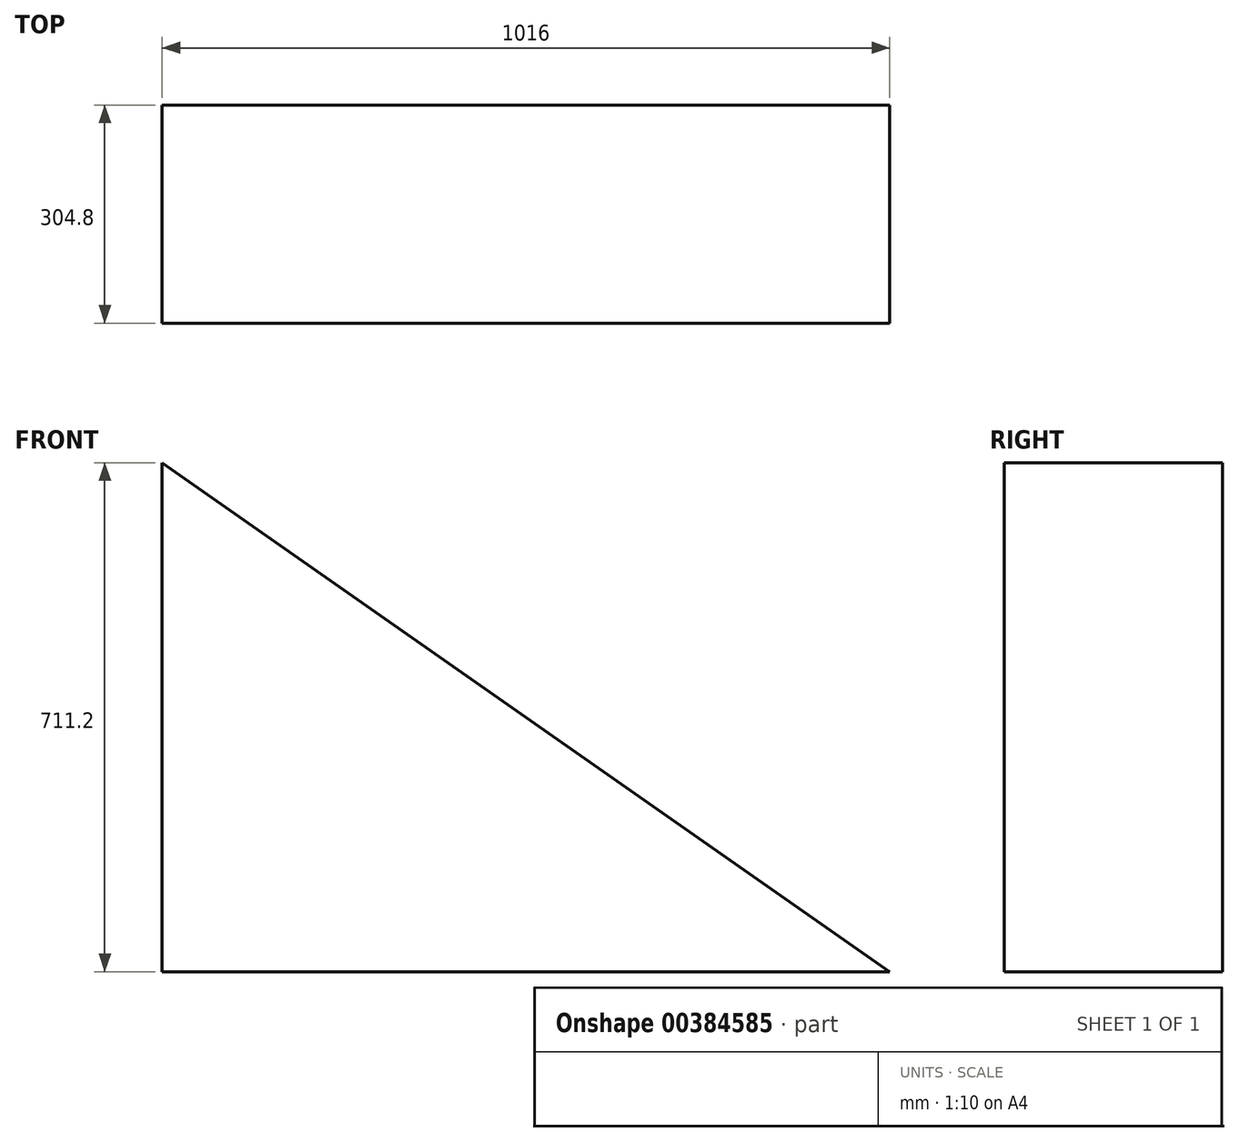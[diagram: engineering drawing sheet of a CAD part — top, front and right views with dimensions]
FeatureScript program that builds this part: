
annotation { "Feature Type Name" : "Feature", "Feature Type Description" : "" }
export const myFeature = defineFeature(function(context is Context, id is Id, definition is map)
    precondition{}
    {
        {
            var Q0;
            Q0=qCreatedBy(makeId("Front.planeOp"),FACE);
            var sketch = newSketch(context, id + "F0", { "sketchPlane" : qUnion([Q0])});
            skLineSegment(sketch, "E0", {"start": v(0, 0) * mm, "end": v(1016, 0) * mm});
            skLineSegment(sketch, "E1", {"start": v(0, 0) * mm, "end": v(0, 711.2) * mm});
            skLineSegment(sketch, "E2", {"start": v(0, 711.2) * mm, "end": v(1016, 0) * mm});
            skSolve(sketch);
        }
        {
            var Q0;
            Q0=makeQuery(id+"F0.imprint","IMPRINT",FACE,{"disambiguationData":[TD([[makeQuery(id+"F0.imprint","IMPRINT",EDGE,{"derivedFrom":sQuery(id+"F0.wireOp",EDGE,"E0")}),1.0]])]});
            extrude(context, id + "F1", {"entities" : qUnion([Q0]), "depth" : 304.8 * mm});
        }
    });
